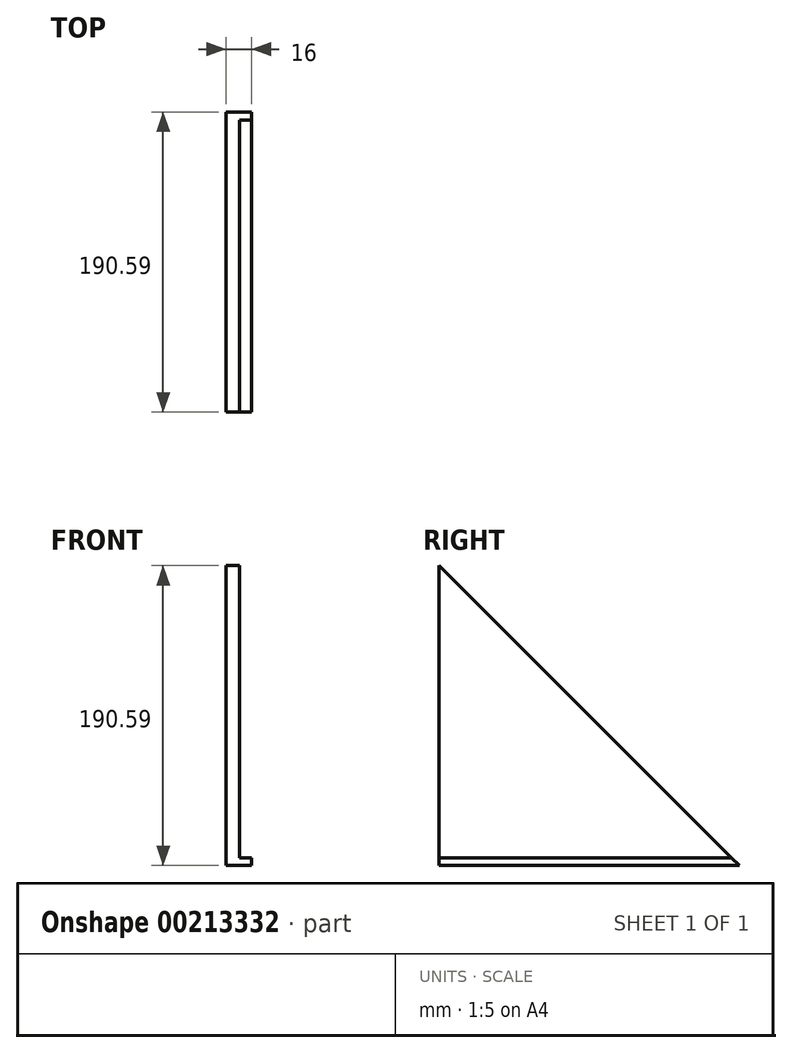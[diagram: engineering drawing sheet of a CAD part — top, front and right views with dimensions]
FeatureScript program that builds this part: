
annotation { "Feature Type Name" : "Feature", "Feature Type Description" : "" }
export const myFeature = defineFeature(function(context is Context, id is Id, definition is map)
    precondition{}
    {
        {
            var Q0;
            Q0=qCreatedBy(makeId("Right.planeOp"),FACE);
            var sketch = newSketch(context, id + "F0", { "sketchPlane" : qUnion([Q0])});
            skLineSegment(sketch, "E0", {"start": v(-57.28, 52.25) * mm, "end": v(-57.28, -138.34) * mm});
            skLineSegment(sketch, "E1", {"start": v(-57.28, -138.34) * mm, "end": v(133.31, -138.34) * mm});
            skLineSegment(sketch, "E2", {"start": v(133.31, -138.34) * mm, "end": v(-57.28, 52.25) * mm});
            skSolve(sketch);
        }
        {
            var Q0;
            Q0=makeQuery(id+"F0.imprint","IMPRINT",FACE,{"disambiguationData":[TD([[makeQuery(id+"F0.imprint","IMPRINT",EDGE,{"derivedFrom":sQuery(id+"F0.wireOp",EDGE,"E0")}),1.0]])]});
            extrude(context, id + "F1", {"entities" : qUnion([Q0]), "depth" : 8.38 * mm});
        }
        {
            var Q0;
            Q0=makeQuery(id+"F1.opExtrude","CAP_FACE",FACE,{"disambiguationData":[OSD([sQuery(id+"F0.wireOp",EDGE,"E0"),sQuery(id+"F0.wireOp",EDGE,"E1"),sQuery(id+"F0.wireOp",EDGE,"E2")])],"isStart":false});
            var sketch = newSketch(context, id + "F2", { "sketchPlane" : qUnion([Q0])});
            skLineSegment(sketch, "E3", {"start": v(-57.28, -138.34) * mm, "end": v(133.31, -138.34) * mm});
            skLineSegment(sketch, "E4", {"start": v(133.31, -138.34) * mm, "end": v(128.31, -133.34) * mm});
            skLineSegment(sketch, "E5", {"start": v(128.31, -133.34) * mm, "end": v(-57.28, -133.34) * mm});
            skLineSegment(sketch, "E6", {"start": v(-57.28, -133.34) * mm, "end": v(-57.28, -138.34) * mm});
            skSolve(sketch);
        }
        {
            var Q0;
            Q0=makeQuery(id+"F2.imprint","IMPRINT",FACE,{"disambiguationData":[TD([[makeQuery(id+"F2.imprint","IMPRINT",EDGE,{"derivedFrom":sQuery(id+"F2.wireOp",EDGE,"E3")}),1.0]])]});
            extrude(context, id + "F3", {"entities" : qUnion([Q0]), "operationType" : NewBodyOperationType.ADD, "depth" : 7.62 * mm});
        }
    });
